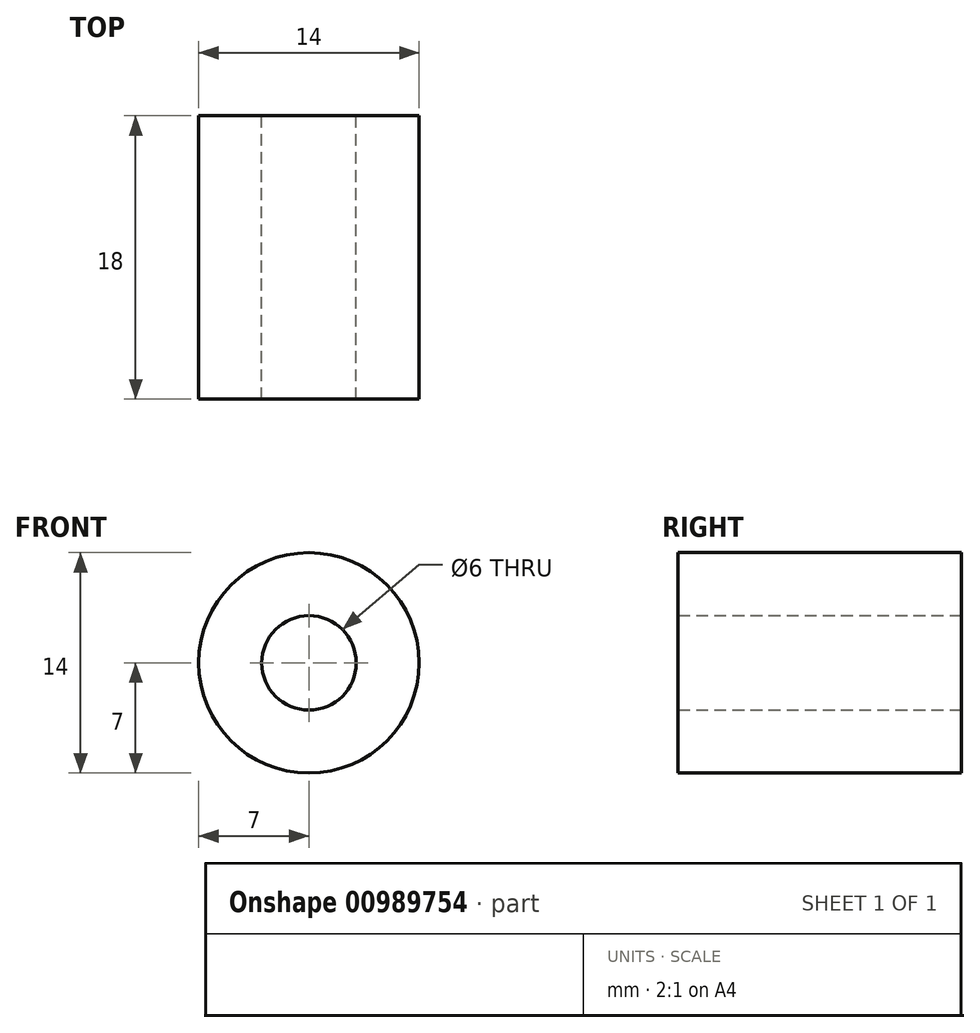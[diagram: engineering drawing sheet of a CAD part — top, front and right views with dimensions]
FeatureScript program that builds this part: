
annotation { "Feature Type Name" : "Feature", "Feature Type Description" : "" }
export const myFeature = defineFeature(function(context is Context, id is Id, definition is map)
    precondition{}
    {
        {
            var Q0;
            Q0=qCreatedBy(makeId("Front.planeOp"),FACE);
            var sketch = newSketch(context, id + "F0", { "sketchPlane" : qUnion([Q0])});
            skCircle(sketch, "E0", {"center": v(0, 0) * mm, "radius": 3 * mm});
            skCircle(sketch, "E1", {"center": v(0, 0) * mm, "radius": 7 * mm});
            skSolve(sketch);
        }
        {
            var Q0;
            Q0=makeQuery(id+"F0.imprint","IMPRINT",FACE,{"disambiguationData":[TD([[makeQuery(id+"F0.imprint","IMPRINT",EDGE,{"derivedFrom":sQuery(id+"F0.wireOp",EDGE,"E0")}),-1.0]])]});
            extrude(context, id + "F1", {"entities" : qUnion([Q0]), "flatOperationType" : FlatOperationType.REMOVE, "depth" : 18 * mm, "offsetDistance" : 25 * mm, "domain" : OperationDomain.MODEL, "symmetric" : true});
        }
    });
